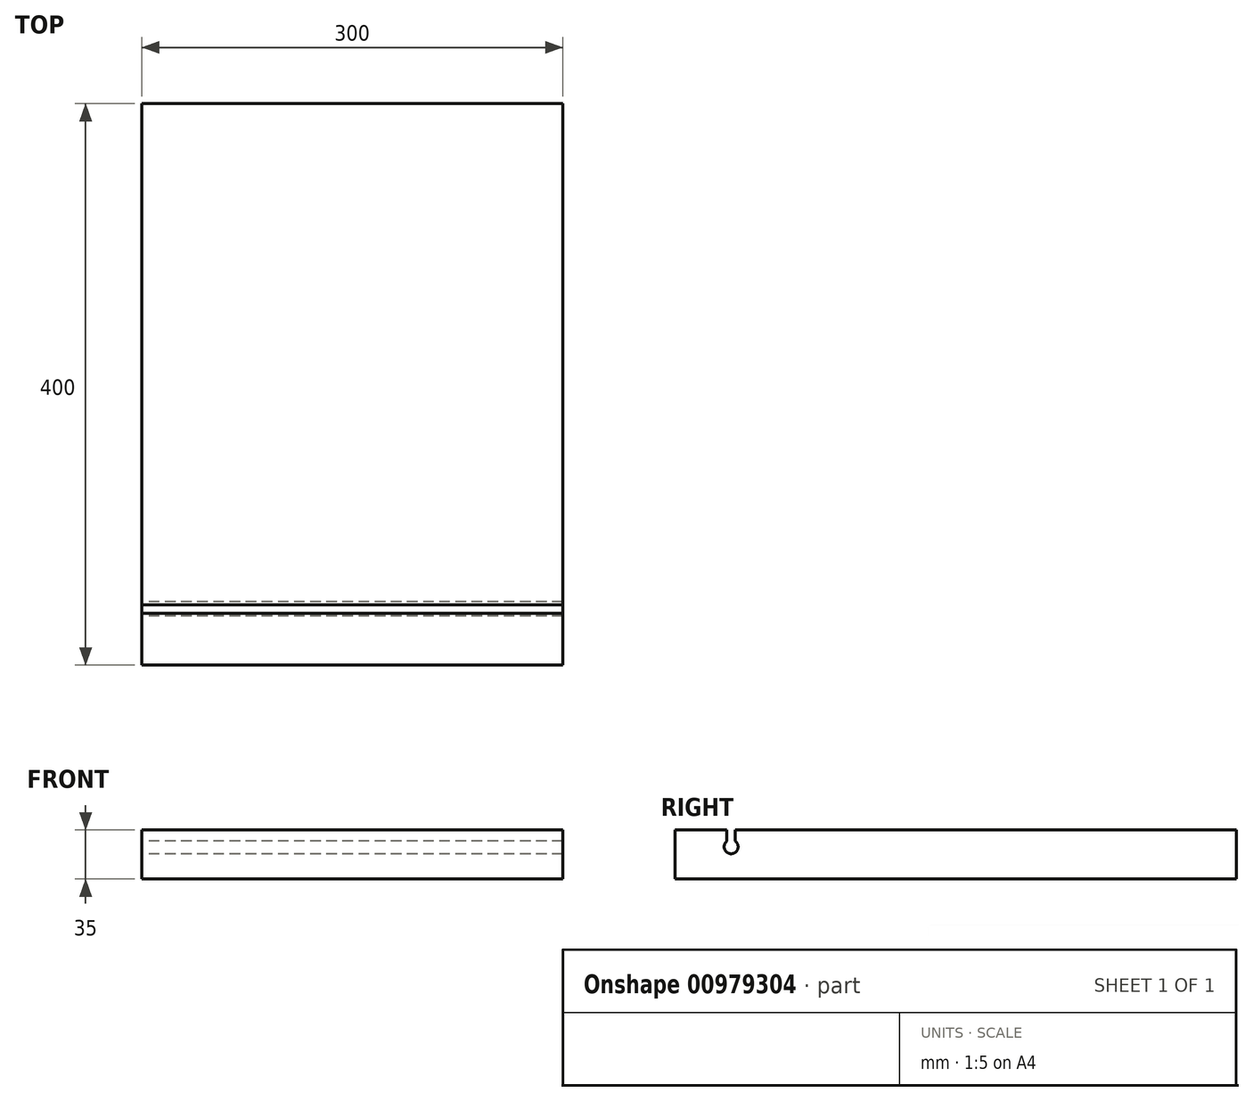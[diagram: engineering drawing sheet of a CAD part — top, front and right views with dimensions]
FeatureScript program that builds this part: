
annotation { "Feature Type Name" : "Feature", "Feature Type Description" : "" }
export const myFeature = defineFeature(function(context is Context, id is Id, definition is map)
    precondition{}
    {
        {
            var Q0;
            Q0=qCreatedBy(makeId("Right.planeOp"),FACE);
            var sketch = newSketch(context, id + "F0", { "sketchPlane" : qUnion([Q0])});
            skLineSegment(sketch, "E0.bottom", {"start": v(0, 0) * mm, "end": v(400, 0) * mm});
            skLineSegment(sketch, "E0.top", {"start": v(0, 35) * mm, "end": v(37, 35) * mm});
            skLineSegment(sketch, "E0.left", {"start": v(0, 0) * mm, "end": v(0, 35) * mm});
            skLineSegment(sketch, "E0.right", {"start": v(400, 0) * mm, "end": v(400, 35) * mm});
            skArc(sketch, "E1", {"start": v(37, 27) * mm, "mid": v(40, 18) * mm, "end": v(43, 27) * mm});
            skLineSegment(sketch, "E2", {"start": v(40, -6.3) * mm, "end": v(40, 73.35) * mm, "construction": true});
            skLineSegment(sketch, "E3", {"start": v(37, 27) * mm, "end": v(37, 35) * mm});
            skLineSegment(sketch, "E4", {"start": v(43, 27) * mm, "end": v(43, 35) * mm});
            skLineSegment(sketch, "E5.trimOffspring", {"start": v(43, 35) * mm, "end": v(400, 35) * mm});
            skSolve(sketch);
        }
        {
            var Q0;
            Q0=makeQuery(id+"F0.imprint","IMPRINT",FACE,{"disambiguationData":[TD([[makeQuery(id+"F0.imprint","IMPRINT",EDGE,{"derivedFrom":sQuery(id+"F0.wireOp",EDGE,"E0.bottom")}),1.0]])]});
            extrude(context, id + "F1", {"entities" : qUnion([Q0]), "depth" : 300 * mm, "offsetDistance" : 25 * mm});
        }
    });
